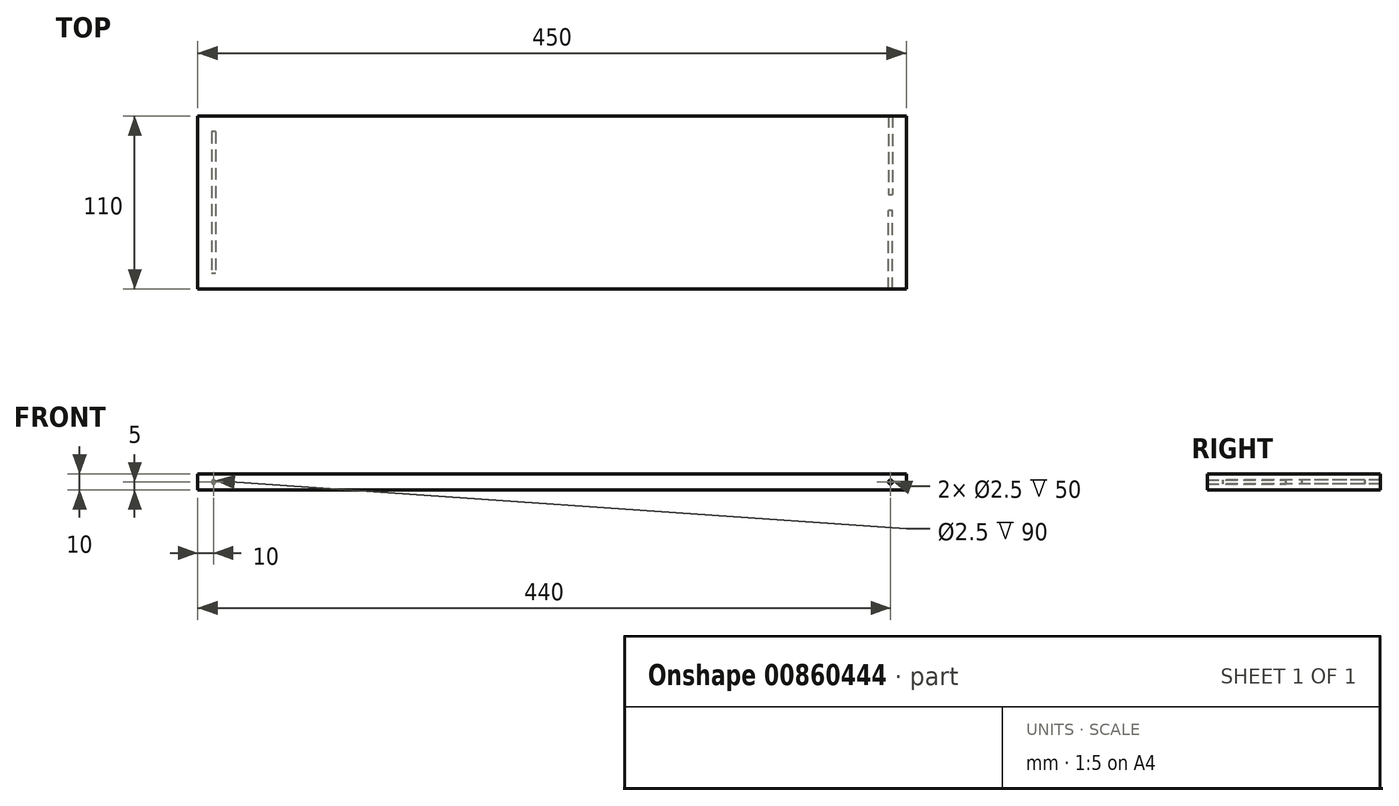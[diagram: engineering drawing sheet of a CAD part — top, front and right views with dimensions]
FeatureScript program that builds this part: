
annotation { "Feature Type Name" : "Feature", "Feature Type Description" : "" }
export const myFeature = defineFeature(function(context is Context, id is Id, definition is map)
    precondition{}
    {
        {
            var Q0;
            Q0=qCreatedBy(makeId("Top.planeOp"),FACE);
            var sketch = newSketch(context, id + "F0", { "sketchPlane" : qUnion([Q0])});
            skLineSegment(sketch, "E0.bottom", {"start": v(-40, 32.34) * mm, "end": v(210, 32.34) * mm});
            skLineSegment(sketch, "E0.top", {"start": v(-40, 22.34) * mm, "end": v(210, 22.34) * mm});
            skLineSegment(sketch, "E0.left", {"start": v(-40, 32.34) * mm, "end": v(-40, 22.34) * mm});
            skLineSegment(sketch, "E0.right", {"start": v(210, 32.34) * mm, "end": v(210, 22.34) * mm});
            skLineSegment(sketch, "E1.bottom", {"start": v(10, -17.66) * mm, "end": v(-240, -17.66) * mm});
            skLineSegment(sketch, "E1.top", {"start": v(10, -27.66) * mm, "end": v(-240, -27.66) * mm});
            skLineSegment(sketch, "E1.left", {"start": v(10, -17.66) * mm, "end": v(10, -27.66) * mm});
            skLineSegment(sketch, "E1.right", {"start": v(-240, -17.66) * mm, "end": v(-240, -27.66) * mm});
            skLineSegment(sketch, "E2.bottom", {"start": v(10, 82.34) * mm, "end": v(-240, 82.34) * mm});
            skLineSegment(sketch, "E2.top", {"start": v(10, 72.34) * mm, "end": v(-240, 72.34) * mm});
            skLineSegment(sketch, "E2.left", {"start": v(10, 82.34) * mm, "end": v(10, 72.34) * mm});
            skLineSegment(sketch, "E2.right", {"start": v(-240, 82.34) * mm, "end": v(-240, 72.34) * mm});
            skSolve(sketch);
        }
        {
            var Q0;
            Q0=makeQuery(id+"F0.imprint","IMPRINT",FACE,{"disambiguationData":[TD([[makeQuery(id+"F0.imprint","IMPRINT",EDGE,{"derivedFrom":sQuery(id+"F0.wireOp",EDGE,"E2.bottom")}),1.0]])]});
            var Q1;
            Q1=makeQuery(id+"F0.imprint","IMPRINT",FACE,{"disambiguationData":[TD([[makeQuery(id+"F0.imprint","IMPRINT",EDGE,{"derivedFrom":sQuery(id+"F0.wireOp",EDGE,"E0.bottom")}),-1.0]])]});
            var Q2;
            Q2=makeQuery(id+"F0.imprint","IMPRINT",FACE,{"disambiguationData":[TD([[makeQuery(id+"F0.imprint","IMPRINT",EDGE,{"derivedFrom":sQuery(id+"F0.wireOp",EDGE,"E1.bottom")}),1.0]])]});
            extrude(context, id + "F1", {"entities" : qUnion([Q0, Q1, Q2]), "endBound" : BoundingType.SYMMETRIC, "depth" : 10 * mm, "offsetDistance" : 25 * mm});
        }
        {
            var Q0;
            Q0=makeQuery(id+"F1.opExtrude","SWEPT_FACE",FACE,{"disambiguationData":[OSD([sQuery(id+"F0.wireOp",EDGE,"E1.top")])]});
            var sketch = newSketch(context, id + "F2", { "sketchPlane" : qUnion([Q0])});
            skLineSegment(sketch, "E3", {"start": v(-30, 5) * mm, "end": v(-30, -5) * mm});
            skLineSegment(sketch, "E4", {"start": v(-30, -5) * mm, "end": v(10, -5) * mm});
            skPoint(sketch, "E5", {"position": v(-10, -5) * mm});
            skPoint(sketch, "E6", {"position": v(-10, 0) * mm});
            skCircle(sketch, "E7", {"center": v(-10, 0) * mm, "radius": 1.25 * mm});
            skSolve(sketch);
        }
        {
            var Q0;
            Q0=makeQuery(id+"F2.imprint","IMPRINT",FACE,{"disambiguationData":[TD([[makeQuery(id+"F2.imprint","IMPRINT",EDGE,{"derivedFrom":sQuery(id+"F2.wireOp",EDGE,"E7")}),1.0]])]});
            extrude(context, id + "F3", {"entities" : qUnion([Q0]), "oppositeDirection" : true, "depth" : 109 * mm, "offsetDistance" : 25 * mm});
        }
        {
            var Q0;
            Q0=makeQuery(id+"F1.opExtrude","SWEPT_FACE",FACE,{"disambiguationData":[OSD([sQuery(id+"F0.wireOp",EDGE,"E1.top")])]});
            var sketch = newSketch(context, id + "F4", { "sketchPlane" : qUnion([Q0])});
            skLineSegment(sketch, "E8", {"start": v(-230, 5) * mm, "end": v(-230, -5) * mm});
            skPoint(sketch, "E9", {"position": v(-230, 0) * mm});
            skCircle(sketch, "E10", {"center": v(-230, 0) * mm, "radius": 1.25 * mm});
            skSolve(sketch);
        }
        {
            var Q0;
            {var subQ0=sQuery(id+"F4.wireOp",EDGE,"E10");var subQ1=sQuery(id+"F4.wireOp",EDGE,"E8");var subQ2=makeQuery(id+"F4.imprint","INTERSECT",VERTEX,{"disambiguationData":[OD(0.0)],"derivedFrom":[subQ1,subQ0]});Q0=makeQuery(id+"F4.imprint","IMPRINT",FACE,{"disambiguationData":[TD([[makeQuery(id+"F4.imprint","IMPRINT",EDGE,{"disambiguationData":[TD([[subQ2,-1.0]])],"derivedFrom":subQ1}),-1.0]])]});}
            var Q1;
            {var subQ0=sQuery(id+"F4.wireOp",EDGE,"E10");var subQ1=sQuery(id+"F4.wireOp",EDGE,"E8");var subQ2=makeQuery(id+"F4.imprint","INTERSECT",VERTEX,{"disambiguationData":[OD(0.0)],"derivedFrom":[subQ1,subQ0]});Q1=makeQuery(id+"F4.imprint","IMPRINT",FACE,{"disambiguationData":[TD([[makeQuery(id+"F4.imprint","IMPRINT",EDGE,{"disambiguationData":[TD([[subQ2,-1.0]])],"derivedFrom":subQ1}),1.0]])]});}
            extrude(context, id + "F5", {"entities" : qUnion([Q0, Q1]), "depth" : -100 * mm, "offsetDistance" : 25 * mm});
        }
        {
            var Q0;
            Q0=makeQuery(id+"F1.opExtrude","SWEPT_FACE",FACE,{"disambiguationData":[OSD([sQuery(id+"F0.wireOp",EDGE,"E0.bottom")])]});
            var sketch = newSketch(context, id + "F6", { "sketchPlane" : qUnion([Q0])});
            skLineSegment(sketch, "E11", {"start": v(-200, 5) * mm, "end": v(-200, -5) * mm});
            skPoint(sketch, "E12", {"position": v(-200, 0) * mm});
            skCircle(sketch, "E13", {"center": v(-200, 0) * mm, "radius": 1.25 * mm});
            skSolve(sketch);
        }
        {
            var Q0;
            {var subQ0=sQuery(id+"F6.wireOp",EDGE,"E13");var subQ1=sQuery(id+"F6.wireOp",EDGE,"E11");var subQ2=makeQuery(id+"F6.imprint","INTERSECT",VERTEX,{"disambiguationData":[OD(0.0)],"derivedFrom":[subQ1,subQ0]});Q0=makeQuery(id+"F6.imprint","IMPRINT",FACE,{"disambiguationData":[TD([[makeQuery(id+"F6.imprint","IMPRINT",EDGE,{"disambiguationData":[TD([[subQ2,-1.0]])],"derivedFrom":subQ1}),1.0]])]});}
            var Q1;
            {var subQ0=sQuery(id+"F6.wireOp",EDGE,"E13");var subQ1=sQuery(id+"F6.wireOp",EDGE,"E11");var subQ2=makeQuery(id+"F6.imprint","INTERSECT",VERTEX,{"disambiguationData":[OD(0.0)],"derivedFrom":[subQ1,subQ0]});Q1=makeQuery(id+"F6.imprint","IMPRINT",FACE,{"disambiguationData":[TD([[makeQuery(id+"F6.imprint","IMPRINT",EDGE,{"disambiguationData":[TD([[subQ2,-1.0]])],"derivedFrom":subQ1}),-1.0]])]});}
            extrude(context, id + "F7", {"entities" : qUnion([Q0, Q1]), "operationType" : NewBodyOperationType.ADD, "depth" : 50 * mm, "offsetDistance" : 25 * mm});
        }
        {
            var Q0;
            Q0=makeQuery(id+"F1.opExtrude","SWEPT_FACE",FACE,{"disambiguationData":[OSD([sQuery(id+"F0.wireOp",EDGE,"E0.top")])]});
            var sketch = newSketch(context, id + "F8", { "sketchPlane" : qUnion([Q0])});
            skLineSegment(sketch, "E14", {"start": v(200, 5) * mm, "end": v(200, -5) * mm});
            skPoint(sketch, "E15", {"position": v(200, 0) * mm});
            skCircle(sketch, "E16", {"center": v(200, 0) * mm, "radius": 1.25 * mm});
            skSolve(sketch);
        }
        {
            var Q0;
            {var subQ0=sQuery(id+"F8.wireOp",EDGE,"E16");var subQ1=sQuery(id+"F8.wireOp",EDGE,"E14");var subQ2=makeQuery(id+"F8.imprint","INTERSECT",VERTEX,{"disambiguationData":[OD(0.0)],"derivedFrom":[subQ1,subQ0]});Q0=makeQuery(id+"F8.imprint","IMPRINT",FACE,{"disambiguationData":[TD([[makeQuery(id+"F8.imprint","IMPRINT",EDGE,{"disambiguationData":[TD([[subQ2,-1.0]])],"derivedFrom":subQ1}),1.0]])]});}
            var Q1;
            {var subQ0=sQuery(id+"F8.wireOp",EDGE,"E16");var subQ1=sQuery(id+"F8.wireOp",EDGE,"E14");var subQ2=makeQuery(id+"F8.imprint","INTERSECT",VERTEX,{"disambiguationData":[OD(0.0)],"derivedFrom":[subQ1,subQ0]});Q1=makeQuery(id+"F8.imprint","IMPRINT",FACE,{"disambiguationData":[TD([[makeQuery(id+"F8.imprint","IMPRINT",EDGE,{"disambiguationData":[TD([[subQ2,-1.0]])],"derivedFrom":subQ1}),-1.0]])]});}
            extrude(context, id + "F9", {"entities" : qUnion([Q0, Q1]), "operationType" : NewBodyOperationType.ADD, "depth" : 50 * mm, "offsetDistance" : 25 * mm});
        }
    });
